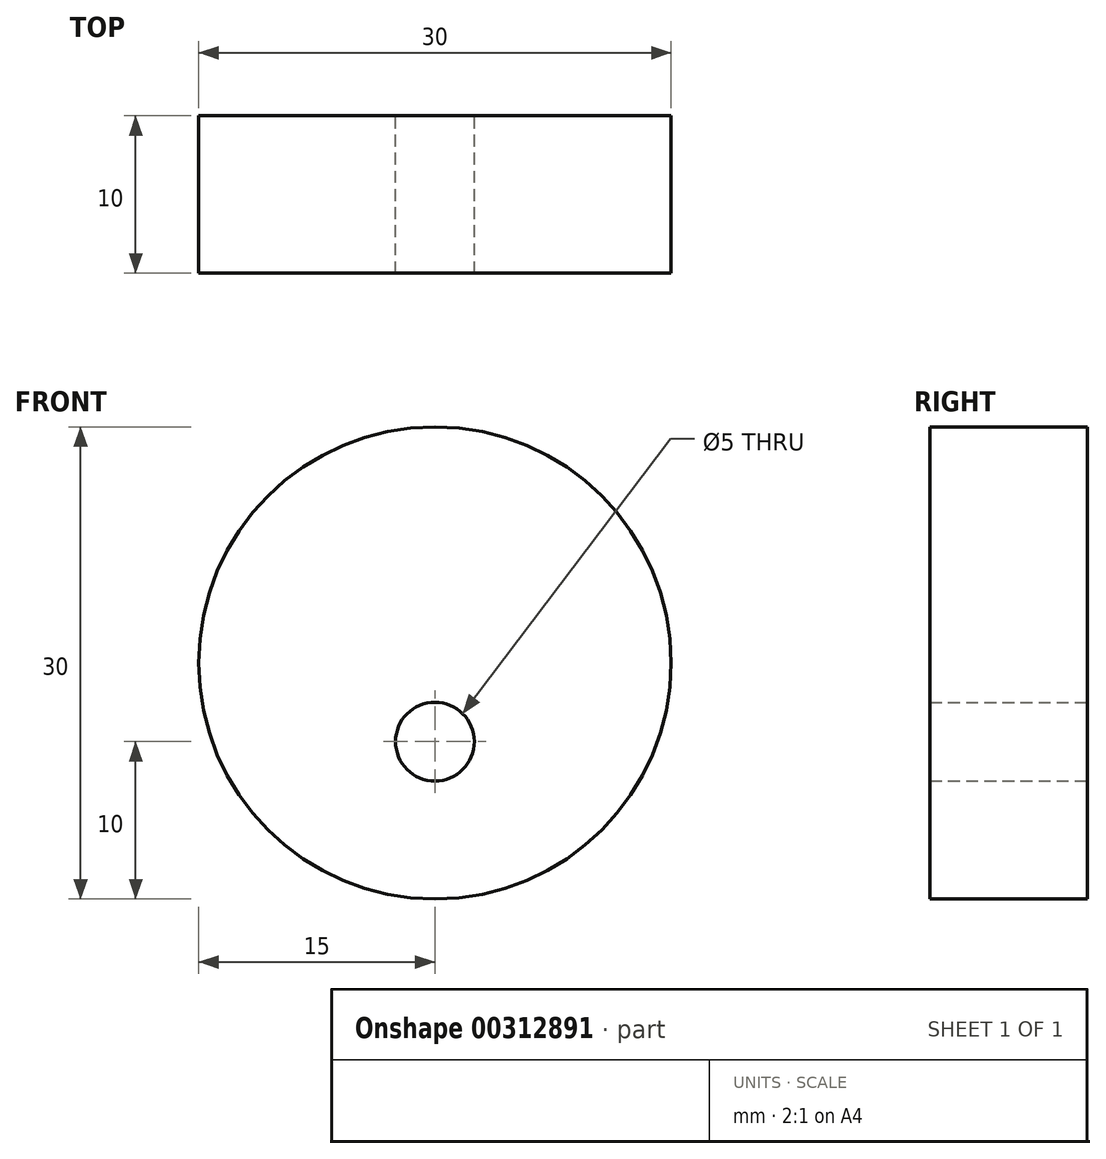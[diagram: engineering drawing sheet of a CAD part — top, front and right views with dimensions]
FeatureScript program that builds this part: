
annotation { "Feature Type Name" : "Feature", "Feature Type Description" : "" }
export const myFeature = defineFeature(function(context is Context, id is Id, definition is map)
    precondition{}
    {
        {
            var Q0;
            Q0=qCreatedBy(makeId("Front.planeOp"),FACE);
            var sketch = newSketch(context, id + "F0", { "sketchPlane" : qUnion([Q0])});
            skCircle(sketch, "E0", {"center": v(0, 0) * mm, "radius": 15 * mm});
            skCircle(sketch, "E1", {"center": v(0, -5) * mm, "radius": 2.5 * mm});
            skSolve(sketch);
        }
        {
            var Q0;
            Q0 = qSketchRegion(id + "F0", true);
            extrude(context, id + "F1", {"entities" : qUnion([Q0]), "depth" : 10 * mm, "offsetDistance" : 25 * mm});
        }
    });
